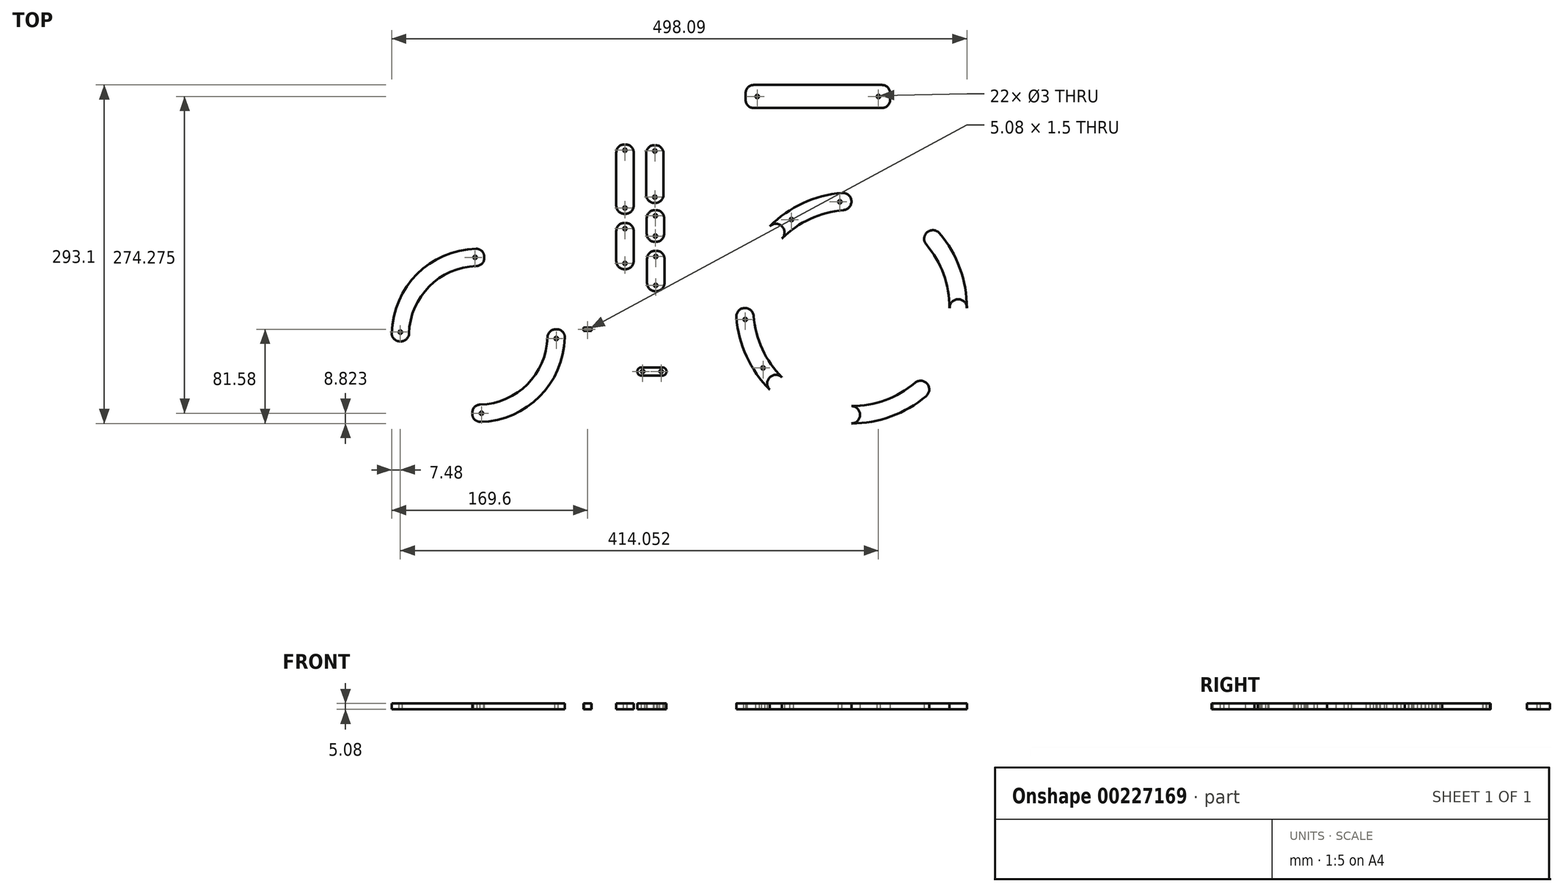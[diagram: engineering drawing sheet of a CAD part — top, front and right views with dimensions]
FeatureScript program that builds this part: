
annotation { "Feature Type Name" : "Feature", "Feature Type Description" : "" }
export const myFeature = defineFeature(function(context is Context, id is Id, definition is map)
    precondition{}
    {
        {
            var Q0;
            Q0=qCreatedBy(makeId("Top.planeOp"),FACE);
            var sketch = newSketch(context, id + "F0", { "sketchPlane" : qUnion([Q0])});
            skCircle(sketch, "E0", {"center": v(-65.55, 15.91) * mm, "radius": 75 * mm});
            skCircle(sketch, "E1", {"center": v(-65.55, 15.91) * mm, "radius": 60 * mm});
            skCircle(sketch, "E2", {"center": v(-68.33, 83.41) * mm, "radius": 1.5 * mm});
            skCircle(sketch, "E3", {"center": v(-133.05, 18.7) * mm, "radius": 1.5 * mm});
            skLineSegment(sketch, "E4", {"start": v(-140.37, 10.7) * mm, "end": v(-125.32, 10.7) * mm});
            skPoint(sketch, "E4.startSnap0", {"position": v(-133.05, 10.7) * mm});
            skLineSegment(sketch, "E5", {"start": v(-60.33, 90.73) * mm, "end": v(-60.33, 75.69) * mm});
            skPoint(sketch, "E5.startSnap0", {"position": v(-60.33, 83.41) * mm});
            skCircle(sketch, "E6", {"center": v(1.95, 13.13) * mm, "radius": 1.5 * mm});
            skCircle(sketch, "E7", {"center": v(-62.77, -51.59) * mm, "radius": 1.5 * mm});
            skLineSegment(sketch, "E8", {"start": v(-70.77, -43.86) * mm, "end": v(-70.77, -58.9) * mm});
            skPoint(sketch, "E8.startSnap0", {"position": v(-70.77, -51.59) * mm});
            skPoint(sketch, "E8.endSnap0", {"position": v(-70.77, -51.59) * mm});
            skPoint(sketch, "E9.startSnap0", {"position": v(1.95, 21.13) * mm});
            skLineSegment(sketch, "E10", {"start": v(-5.78, 21.13) * mm, "end": v(9.27, 21.13) * mm});
            skLineSegment(sketch, "E11.bottom", {"start": v(32.57, 19.67) * mm, "end": v(25.57, 19.67) * mm});
            skLineSegment(sketch, "E11.top", {"start": v(32.57, 22.67) * mm, "end": v(25.57, 22.67) * mm});
            skLineSegment(sketch, "E11.left", {"start": v(32.57, 19.67) * mm, "end": v(32.57, 22.67) * mm});
            skLineSegment(sketch, "E11.right", {"start": v(25.57, 19.67) * mm, "end": v(25.57, 22.67) * mm});
            skPoint(sketch, "E11.middle", {"position": v(29.07, 21.17) * mm});
            skLineSegment(sketch, "E12.bottom", {"start": v(31.61, 21.92) * mm, "end": v(26.53, 21.92) * mm});
            skLineSegment(sketch, "E12.top", {"start": v(31.61, 20.42) * mm, "end": v(26.53, 20.42) * mm});
            skLineSegment(sketch, "E12.left", {"start": v(31.61, 21.92) * mm, "end": v(31.61, 20.42) * mm});
            skLineSegment(sketch, "E12.right", {"start": v(26.53, 21.92) * mm, "end": v(26.53, 20.42) * mm});
            skLineSegment(sketch, "E13.bottom", {"start": v(97.3, -11.9) * mm, "end": v(72.3, -11.9) * mm});
            skLineSegment(sketch, "E13.top", {"start": v(97.3, -18.9) * mm, "end": v(72.3, -18.9) * mm});
            skLineSegment(sketch, "E13.left", {"start": v(97.3, -11.9) * mm, "end": v(97.3, -18.9) * mm});
            skLineSegment(sketch, "E13.right", {"start": v(72.3, -11.9) * mm, "end": v(72.3, -18.9) * mm});
            skPoint(sketch, "E13.middle", {"position": v(84.8, -15.4) * mm});
            skCircle(sketch, "E14", {"center": v(92.8, -15.4) * mm, "radius": 1.5 * mm});
            skLineSegment(sketch, "E15", {"start": v(84.8, -11.9) * mm, "end": v(84.8, -18.9) * mm});
            skCircle(sketch, "E16.MirrorC", {"center": v(76.8, -15.4) * mm, "radius": 1.5 * mm});
            skCircle(sketch, "E17", {"center": v(257.56, 39.59) * mm, "radius": 100 * mm});
            skCircle(sketch, "E18", {"center": v(257.56, 39.59) * mm, "radius": 85 * mm});
            skLineSegment(sketch, "E19", {"start": v(257.56, 39.59) * mm, "end": v(257.56, 139.59) * mm});
            skLineSegment(sketch, "E20", {"start": v(257.56, 39.59) * mm, "end": v(157.56, 39.59) * mm});
            skLineSegment(sketch, "E21", {"start": v(257.56, 39.59) * mm, "end": v(257.56, -60.41) * mm});
            skLineSegment(sketch, "E22", {"start": v(257.56, 39.59) * mm, "end": v(357.56, 39.59) * mm});
            skLineSegment(sketch, "E23", {"start": v(257.56, 39.59) * mm, "end": v(186.85, 110.3) * mm});
            skLineSegment(sketch, "E24.MirrorCS", {"start": v(257.56, 39.59) * mm, "end": v(328.28, 110.3) * mm});
            skLineSegment(sketch, "E25.MirrorCS", {"start": v(257.56, 39.59) * mm, "end": v(328.28, -31.13) * mm});
            skLineSegment(sketch, "E26.MirrorCS", {"start": v(257.56, 39.59) * mm, "end": v(186.85, -31.13) * mm});
            skArc(sketch, "E27", {"start": v(197.46, -20.52) * mm, "mid": v(186.85, -20.52) * mm, "end": v(186.85, -31.13) * mm});
            skArc(sketch, "E28", {"start": v(257.56, -60.41) * mm, "mid": v(265.06, -52.91) * mm, "end": v(257.56, -45.41) * mm});
            skArc(sketch, "E29", {"start": v(357.56, 39.59) * mm, "mid": v(350.06, 47.09) * mm, "end": v(342.56, 39.59) * mm});
            skArc(sketch, "E30", {"start": v(197.46, 99.69) * mm, "mid": v(197.46, 110.3) * mm, "end": v(186.85, 110.3) * mm});
            skCircle(sketch, "E31", {"center": v(257.56, 39.59) * mm, "radius": 92.5 * mm, "construction": true});
            skCircle(sketch, "E32", {"center": v(205.65, 116.14) * mm, "radius": 1.5 * mm});
            skCircle(sketch, "E33", {"center": v(247.56, 131.54) * mm, "radius": 1.5 * mm});
            skCircle(sketch, "E34", {"center": v(181, -12.33) * mm, "radius": 1.5 * mm});
            skCircle(sketch, "E35", {"center": v(165.6, 29.59) * mm, "radius": 1.5 * mm});
            skLineSegment(sketch, "E36.bottom", {"start": v(53.97, 181.17) * mm, "end": v(68.97, 181.17) * mm});
            skLineSegment(sketch, "E36.top", {"start": v(53.97, 121.17) * mm, "end": v(68.97, 121.17) * mm});
            skLineSegment(sketch, "E36.left", {"start": v(53.97, 181.17) * mm, "end": v(53.97, 121.17) * mm});
            skLineSegment(sketch, "E36.right", {"start": v(68.97, 181.17) * mm, "end": v(68.97, 121.17) * mm});
            skLineSegment(sketch, "E37.bottom", {"start": v(53.97, 113.23) * mm, "end": v(68.97, 113.23) * mm});
            skLineSegment(sketch, "E37.top", {"start": v(53.97, 73.23) * mm, "end": v(68.97, 73.23) * mm});
            skLineSegment(sketch, "E37.left", {"start": v(53.97, 113.23) * mm, "end": v(53.97, 73.23) * mm});
            skLineSegment(sketch, "E37.right", {"start": v(68.97, 113.23) * mm, "end": v(68.97, 73.23) * mm});
            skLineSegment(sketch, "E38.bottom", {"start": v(80.64, 89.11) * mm, "end": v(95.64, 89.11) * mm});
            skLineSegment(sketch, "E38.top", {"start": v(80.64, 54.11) * mm, "end": v(95.64, 54.11) * mm});
            skLineSegment(sketch, "E38.left", {"start": v(80.64, 89.11) * mm, "end": v(80.64, 54.11) * mm});
            skLineSegment(sketch, "E38.right", {"start": v(95.64, 89.11) * mm, "end": v(95.64, 54.11) * mm});
            skCircle(sketch, "E39", {"center": v(61.47, 176.17) * mm, "radius": 1.5 * mm});
            skPoint(sketch, "E39.centerSnap0", {"position": v(61.47, 181.17) * mm});
            skLineSegment(sketch, "E40", {"start": v(53.97, 151.17) * mm, "end": v(68.97, 151.17) * mm, "construction": true});
            skCircle(sketch, "E41.MirrorC", {"center": v(61.47, 126.17) * mm, "radius": 1.5 * mm});
            skCircle(sketch, "E42", {"center": v(88.14, 84.11) * mm, "radius": 1.5 * mm});
            skPoint(sketch, "E42.centerSnap0", {"position": v(88.14, 89.11) * mm});
            skLineSegment(sketch, "E43", {"start": v(80.64, 71.61) * mm, "end": v(95.64, 71.61) * mm, "construction": true});
            skCircle(sketch, "E44.MirrorC", {"center": v(88.14, 59.11) * mm, "radius": 1.5 * mm});
            skLineSegment(sketch, "E45", {"start": v(53.97, 93.23) * mm, "end": v(68.97, 93.23) * mm, "construction": true});
            skCircle(sketch, "E46", {"center": v(61.47, 108.23) * mm, "radius": 1.5 * mm});
            skPoint(sketch, "E46.centerSnap0", {"position": v(61.47, 113.23) * mm});
            skCircle(sketch, "E47.MirrorC", {"center": v(61.47, 78.23) * mm, "radius": 1.5 * mm});
            skPoint(sketch, "E48.centerSnap0", {"position": v(114.78, 118.5) * mm});
            skLineSegment(sketch, "E49", {"start": v(87.84, 119.35) * mm, "end": v(87.84, 101.85) * mm});
            skCircle(sketch, "E50", {"center": v(87.84, 119.35) * mm, "radius": 1.5 * mm});
            skCircle(sketch, "E51", {"center": v(87.84, 101.85) * mm, "radius": 1.5 * mm});
            skLineSegment(sketch, "E52.bottom", {"start": v(95.34, 124.35) * mm, "end": v(80.34, 124.35) * mm});
            skLineSegment(sketch, "E52.top", {"start": v(95.34, 96.85) * mm, "end": v(80.34, 96.85) * mm});
            skLineSegment(sketch, "E52.left", {"start": v(95.34, 124.35) * mm, "end": v(95.34, 96.85) * mm});
            skLineSegment(sketch, "E52.right", {"start": v(80.34, 124.35) * mm, "end": v(80.34, 96.85) * mm});
            skPoint(sketch, "E52.middle", {"position": v(87.84, 110.6) * mm});
            skLineSegment(sketch, "E53.bottom", {"start": v(79.83, 180.55) * mm, "end": v(94.83, 180.55) * mm});
            skLineSegment(sketch, "E53.top", {"start": v(79.83, 130.55) * mm, "end": v(94.83, 130.55) * mm});
            skLineSegment(sketch, "E53.left", {"start": v(79.83, 180.55) * mm, "end": v(79.83, 130.55) * mm});
            skLineSegment(sketch, "E53.right", {"start": v(94.83, 180.55) * mm, "end": v(94.83, 130.55) * mm});
            skCircle(sketch, "E54", {"center": v(87.33, 175.55) * mm, "radius": 1.5 * mm});
            skPoint(sketch, "E54.centerSnap0", {"position": v(87.33, 180.55) * mm});
            skLineSegment(sketch, "E55", {"start": v(79.83, 155.55) * mm, "end": v(94.83, 155.55) * mm, "construction": true});
            skCircle(sketch, "E56.MirrorC", {"center": v(87.33, 135.55) * mm, "radius": 1.5 * mm});
            skLineSegment(sketch, "E57.bottom", {"start": v(166, 232.69) * mm, "end": v(291, 232.69) * mm});
            skLineSegment(sketch, "E57.top", {"start": v(166, 212.69) * mm, "end": v(291, 212.69) * mm});
            skLineSegment(sketch, "E57.left", {"start": v(166, 232.69) * mm, "end": v(166, 212.69) * mm});
            skLineSegment(sketch, "E57.right", {"start": v(291, 232.69) * mm, "end": v(291, 212.69) * mm});
            skCircle(sketch, "E58", {"center": v(176, 222.69) * mm, "radius": 1.5 * mm});
            skPoint(sketch, "E58.centerSnap0", {"position": v(166, 222.69) * mm});
            skLineSegment(sketch, "E59", {"start": v(228.5, 232.69) * mm, "end": v(228.5, 212.69) * mm, "construction": true});
            skCircle(sketch, "E60.MirrorC", {"center": v(281, 222.69) * mm, "radius": 1.5 * mm});
            skSolve(sketch);
        }
        {
            var Q0;
            {var subQ0=sQuery(id+"F0.wireOp",EDGE,"hphmZsM6-x4Mk-0MsM-bUp3-fff5A3cwXpPa");Q0=makeQuery(id+"F0.imprint","IMPRINT",FACE,{"disambiguationData":[TD([[makeQuery(id+"F0.imprint","IMPRINT",EDGE,{"derivedFrom":subQ0}),1.0]])]});}
            var Q1;
            Q1=makeQuery(id+"F0.imprint","IMPRINT",FACE,{"disambiguationData":[TD([[makeQuery(id+"F0.imprint","IMPRINT",EDGE,{"derivedFrom":sQuery(id+"F0.wireOp",EDGE,"E2")}),-1.0]])]});
            var Q2;
            Q2=makeQuery(id+"F0.imprint","IMPRINT",FACE,{"disambiguationData":[TD([[makeQuery(id+"F0.imprint","IMPRINT",EDGE,{"derivedFrom":sQuery(id+"F0.wireOp",EDGE,"E6")}),-1.0]])]});
            var Q3;
            {var subQ0=sQuery(id+"F0.wireOp",EDGE,"E9");Q3=makeQuery(id+"F0.imprint","IMPRINT",FACE,{"disambiguationData":[TD([[makeQuery(id+"F0.imprint","IMPRINT",EDGE,{"derivedFrom":subQ0}),1.0]])]});}
            var Q4;
            Q4=makeQuery(id+"F0.imprint","IMPRINT",FACE,{"disambiguationData":[TD([[makeQuery(id+"F0.imprint","IMPRINT",EDGE,{"derivedFrom":sQuery(id+"F0.wireOp",EDGE,"E11.bottom")}),-1.0]])]});
            var Q5;
            {var subQ1=sQuery(id+"F0.wireOp",EDGE,"E13.right");Q5=makeQuery(id+"F0.imprint","IMPRINT",FACE,{"disambiguationData":[TD([[makeQuery(id+"F0.imprint","IMPRINT",EDGE,{"derivedFrom":subQ1}),1.0]])]});}
            var Q6;
            {var subQ0=sQuery(id+"F0.wireOp",EDGE,"E13.left");Q6=makeQuery(id+"F0.imprint","IMPRINT",FACE,{"disambiguationData":[TD([[makeQuery(id+"F0.imprint","IMPRINT",EDGE,{"derivedFrom":subQ0}),-1.0]])]});}
            var Q7;
            {var subQ0=sQuery(id+"F0.wireOp",EDGE,"E19");var subQ1=sQuery(id+"F0.wireOp",EDGE,"E17");var subQ2=makeQuery(id+"F0.imprint","INTERSECT",VERTEX,{"derivedFrom":[subQ1,subQ0]});Q7=makeQuery(id+"F0.imprint","IMPRINT",FACE,{"disambiguationData":[TD([[makeQuery(id+"F0.imprint","IMPRINT",EDGE,{"disambiguationData":[TD([[subQ2,-1.0]])],"derivedFrom":subQ1}),1.0]])]});}
            var Q8;
            {var subQ0=sQuery(id+"F0.wireOp",EDGE,"E22");var subQ1=sQuery(id+"F0.wireOp",EDGE,"E17");var subQ2=makeQuery(id+"F0.imprint","INTERSECT",VERTEX,{"derivedFrom":[subQ1,subQ0]});Q8=makeQuery(id+"F0.imprint","IMPRINT",FACE,{"disambiguationData":[TD([[makeQuery(id+"F0.imprint","IMPRINT",EDGE,{"disambiguationData":[TD([[subQ2,-1.0]])],"derivedFrom":subQ1}),1.0]])]});}
            var Q9;
            {var subQ0=sQuery(id+"F0.wireOp",EDGE,"E20");var subQ1=sQuery(id+"F0.wireOp",EDGE,"E17");var subQ2=makeQuery(id+"F0.imprint","INTERSECT",VERTEX,{"derivedFrom":[subQ1,subQ0]});Q9=makeQuery(id+"F0.imprint","IMPRINT",FACE,{"disambiguationData":[TD([[makeQuery(id+"F0.imprint","IMPRINT",EDGE,{"disambiguationData":[TD([[subQ2,-1.0]])],"derivedFrom":subQ1}),1.0]])]});}
            var Q10;
            {var subQ0=sQuery(id+"F0.wireOp",EDGE,"E21");var subQ1=sQuery(id+"F0.wireOp",EDGE,"E17");var subQ2=makeQuery(id+"F0.imprint","INTERSECT",VERTEX,{"derivedFrom":[subQ1,subQ0]});Q10=makeQuery(id+"F0.imprint","IMPRINT",FACE,{"disambiguationData":[TD([[makeQuery(id+"F0.imprint","IMPRINT",EDGE,{"disambiguationData":[TD([[subQ2,-1.0]])],"derivedFrom":subQ1}),1.0]])]});}
            var Q11;
            Q11=makeQuery(id+"F0.imprint","IMPRINT",FACE,{"disambiguationData":[TD([[makeQuery(id+"F0.imprint","IMPRINT",EDGE,{"derivedFrom":sQuery(id+"F0.wireOp",EDGE,"E36.bottom")}),-1.0]])]});
            var Q12;
            Q12=makeQuery(id+"F0.imprint","IMPRINT",FACE,{"disambiguationData":[TD([[makeQuery(id+"F0.imprint","IMPRINT",EDGE,{"derivedFrom":sQuery(id+"F0.wireOp",EDGE,"E37.bottom")}),-1.0]])]});
            var Q13;
            Q13=makeQuery(id+"F0.imprint","IMPRINT",FACE,{"disambiguationData":[TD([[makeQuery(id+"F0.imprint","IMPRINT",EDGE,{"derivedFrom":sQuery(id+"F0.wireOp",EDGE,"E38.bottom")}),-1.0]])]});
            var Q14;
            Q14=makeQuery(id+"F0.imprint","IMPRINT",FACE,{"disambiguationData":[TD([[makeQuery(id+"F0.imprint","IMPRINT",EDGE,{"derivedFrom":sQuery(id+"F0.wireOp",EDGE,"E50")}),-1.0]])]});
            var Q15;
            Q15=makeQuery(id+"F0.imprint","IMPRINT",FACE,{"disambiguationData":[TD([[makeQuery(id+"F0.imprint","IMPRINT",EDGE,{"derivedFrom":sQuery(id+"F0.wireOp",EDGE,"E53.bottom")}),-1.0]])]});
            var Q16;
            Q16=makeQuery(id+"F0.imprint","IMPRINT",FACE,{"disambiguationData":[TD([[makeQuery(id+"F0.imprint","IMPRINT",EDGE,{"derivedFrom":sQuery(id+"F0.wireOp",EDGE,"E57.bottom")}),-1.0]])]});
            extrude(context, id + "F1", {"entities" : qUnion([Q0, Q1, Q2, Q3, Q4, Q5, Q6, Q7, Q8, Q9, Q10, Q11, Q12, Q13, Q14, Q15, Q16]), "depth" : 5.08 * mm, "offsetDistance" : 25 * mm});
        }
        {
            var Q0;
            Q0=makeQuery(id+"F1.opExtrude","SWEPT_EDGE",EDGE,{"disambiguationData":[OSD([sQuery(id+"F0.wireOp",EDGE,"E0"),sQuery(id+"F0.wireOp",EDGE,"E4")])]});
            var Q1;
            Q1=makeQuery(id+"F1.opExtrude","SWEPT_EDGE",EDGE,{"disambiguationData":[OSD([sQuery(id+"F0.wireOp",EDGE,"E1"),sQuery(id+"F0.wireOp",EDGE,"E4")])]});
            var Q2;
            Q2=makeQuery(id+"F1.opExtrude","SWEPT_EDGE",EDGE,{"disambiguationData":[OSD([sQuery(id+"F0.wireOp",EDGE,"E0"),sQuery(id+"F0.wireOp",EDGE,"E5")])]});
            var Q3;
            Q3=makeQuery(id+"F1.opExtrude","SWEPT_EDGE",EDGE,{"disambiguationData":[OSD([sQuery(id+"F0.wireOp",EDGE,"E1"),sQuery(id+"F0.wireOp",EDGE,"E5")])]});
            var Q4;
            Q4=makeQuery(id+"F1.opExtrude","SWEPT_EDGE",EDGE,{"disambiguationData":[OSD([sQuery(id+"F0.wireOp",EDGE,"E1"),sQuery(id+"F0.wireOp",EDGE,"E10")])]});
            var Q5;
            Q5=makeQuery(id+"F1.opExtrude","SWEPT_EDGE",EDGE,{"disambiguationData":[OSD([sQuery(id+"F0.wireOp",EDGE,"E0"),sQuery(id+"F0.wireOp",EDGE,"E10")])]});
            var Q6;
            Q6=makeQuery(id+"F1.opExtrude","SWEPT_EDGE",EDGE,{"disambiguationData":[OSD([sQuery(id+"F0.wireOp",EDGE,"E1"),sQuery(id+"F0.wireOp",EDGE,"E8")])]});
            var Q7;
            Q7=makeQuery(id+"F1.opExtrude","SWEPT_EDGE",EDGE,{"disambiguationData":[OSD([sQuery(id+"F0.wireOp",EDGE,"E0"),sQuery(id+"F0.wireOp",EDGE,"E8")])]});
            var Q8;
            Q8=makeQuery(id+"F1.opExtrude","SWEPT_EDGE",EDGE,{"disambiguationData":[OSD([sQuery(id+"F0.wireOp",EDGE,"E36.bottom"),sQuery(id+"F0.wireOp",EDGE,"E36.right")])]});
            var Q9;
            Q9=makeQuery(id+"F1.opExtrude","SWEPT_EDGE",EDGE,{"disambiguationData":[OSD([sQuery(id+"F0.wireOp",EDGE,"E36.bottom"),sQuery(id+"F0.wireOp",EDGE,"E36.left")])]});
            var Q10;
            Q10=makeQuery(id+"F1.opExtrude","SWEPT_EDGE",EDGE,{"disambiguationData":[OSD([sQuery(id+"F0.wireOp",EDGE,"E36.top"),sQuery(id+"F0.wireOp",EDGE,"E36.left")])]});
            var Q11;
            Q11=makeQuery(id+"F1.opExtrude","SWEPT_EDGE",EDGE,{"disambiguationData":[OSD([sQuery(id+"F0.wireOp",EDGE,"E36.top"),sQuery(id+"F0.wireOp",EDGE,"E36.right")])]});
            var Q12;
            Q12=makeQuery(id+"F1.opExtrude","SWEPT_EDGE",EDGE,{"disambiguationData":[OSD([sQuery(id+"F0.wireOp",EDGE,"E37.bottom"),sQuery(id+"F0.wireOp",EDGE,"E37.left")])]});
            var Q13;
            Q13=makeQuery(id+"F1.opExtrude","SWEPT_EDGE",EDGE,{"disambiguationData":[OSD([sQuery(id+"F0.wireOp",EDGE,"E37.bottom"),sQuery(id+"F0.wireOp",EDGE,"E37.right")])]});
            var Q14;
            Q14=makeQuery(id+"F1.opExtrude","SWEPT_EDGE",EDGE,{"disambiguationData":[OSD([sQuery(id+"F0.wireOp",EDGE,"E37.top"),sQuery(id+"F0.wireOp",EDGE,"E37.right")])]});
            var Q15;
            Q15=makeQuery(id+"F1.opExtrude","SWEPT_EDGE",EDGE,{"disambiguationData":[OSD([sQuery(id+"F0.wireOp",EDGE,"E37.top"),sQuery(id+"F0.wireOp",EDGE,"E37.left")])]});
            var Q16;
            Q16=makeQuery(id+"F1.opExtrude","SWEPT_EDGE",EDGE,{"disambiguationData":[OSD([sQuery(id+"F0.wireOp",EDGE,"E38.top"),sQuery(id+"F0.wireOp",EDGE,"E38.right")])]});
            var Q17;
            Q17=makeQuery(id+"F1.opExtrude","SWEPT_EDGE",EDGE,{"disambiguationData":[OSD([sQuery(id+"F0.wireOp",EDGE,"E38.top"),sQuery(id+"F0.wireOp",EDGE,"E38.left")])]});
            var Q18;
            Q18=makeQuery(id+"F1.opExtrude","SWEPT_EDGE",EDGE,{"disambiguationData":[OSD([sQuery(id+"F0.wireOp",EDGE,"E38.bottom"),sQuery(id+"F0.wireOp",EDGE,"E38.left")])]});
            var Q19;
            Q19=makeQuery(id+"F1.opExtrude","SWEPT_EDGE",EDGE,{"disambiguationData":[OSD([sQuery(id+"F0.wireOp",EDGE,"E38.bottom"),sQuery(id+"F0.wireOp",EDGE,"E38.right")])]});
            var Q20;
            Q20=makeQuery(id+"F1.opExtrude","SWEPT_EDGE",EDGE,{"disambiguationData":[OSD([sQuery(id+"F0.wireOp",EDGE,"E52.bottom"),sQuery(id+"F0.wireOp",EDGE,"E52.right")])]});
            var Q21;
            Q21=makeQuery(id+"F1.opExtrude","SWEPT_EDGE",EDGE,{"disambiguationData":[OSD([sQuery(id+"F0.wireOp",EDGE,"E52.bottom"),sQuery(id+"F0.wireOp",EDGE,"E52.left")])]});
            var Q22;
            Q22=makeQuery(id+"F1.opExtrude","SWEPT_EDGE",EDGE,{"disambiguationData":[OSD([sQuery(id+"F0.wireOp",EDGE,"E52.top"),sQuery(id+"F0.wireOp",EDGE,"E52.left")])]});
            var Q23;
            Q23=makeQuery(id+"F1.opExtrude","SWEPT_EDGE",EDGE,{"disambiguationData":[OSD([sQuery(id+"F0.wireOp",EDGE,"E52.top"),sQuery(id+"F0.wireOp",EDGE,"E52.right")])]});
            var Q24;
            Q24=makeQuery(id+"F1.opExtrude","SWEPT_EDGE",EDGE,{"disambiguationData":[OSD([sQuery(id+"F0.wireOp",EDGE,"E53.top"),sQuery(id+"F0.wireOp",EDGE,"E53.right")])]});
            var Q25;
            Q25=makeQuery(id+"F1.opExtrude","SWEPT_EDGE",EDGE,{"disambiguationData":[OSD([sQuery(id+"F0.wireOp",EDGE,"E53.top"),sQuery(id+"F0.wireOp",EDGE,"E53.left")])]});
            var Q26;
            Q26=makeQuery(id+"F1.opExtrude","SWEPT_EDGE",EDGE,{"disambiguationData":[OSD([sQuery(id+"F0.wireOp",EDGE,"E53.bottom"),sQuery(id+"F0.wireOp",EDGE,"E53.left")])]});
            var Q27;
            Q27=makeQuery(id+"F1.opExtrude","SWEPT_EDGE",EDGE,{"disambiguationData":[OSD([sQuery(id+"F0.wireOp",EDGE,"E53.bottom"),sQuery(id+"F0.wireOp",EDGE,"E53.right")])]});
            var Q28;
            Q28=makeQuery(id+"F1.opExtrude","SWEPT_EDGE",EDGE,{"disambiguationData":[OSD([sQuery(id+"F0.wireOp",EDGE,"E57.bottom"),sQuery(id+"F0.wireOp",EDGE,"E57.left")])]});
            var Q29;
            Q29=makeQuery(id+"F1.opExtrude","SWEPT_EDGE",EDGE,{"disambiguationData":[OSD([sQuery(id+"F0.wireOp",EDGE,"E57.top"),sQuery(id+"F0.wireOp",EDGE,"E57.left")])]});
            var Q30;
            Q30=makeQuery(id+"F1.opExtrude","SWEPT_EDGE",EDGE,{"disambiguationData":[OSD([sQuery(id+"F0.wireOp",EDGE,"E57.bottom"),sQuery(id+"F0.wireOp",EDGE,"E57.right")])]});
            var Q31;
            Q31=makeQuery(id+"F1.opExtrude","SWEPT_EDGE",EDGE,{"disambiguationData":[OSD([sQuery(id+"F0.wireOp",EDGE,"E57.top"),sQuery(id+"F0.wireOp",EDGE,"E57.right")])]});
            fillet(context, id + "F2", {"entities" : qUnion([Q0, Q1, Q2, Q3, Q4, Q5, Q6, Q7, Q8, Q9, Q10, Q11, Q12, Q13, Q14, Q15, Q16, Q17, Q18, Q19, Q20, Q21, Q22, Q23, Q24, Q25, Q26, Q27, Q28, Q29, Q30, Q31]), "radius" : 7 * mm, "tangentPropagation" : true, "allowEdgeOverflow" : false});
        }
        {
            var Q0;
            Q0=makeQuery(id+"F1.opExtrude","SWEPT_EDGE",EDGE,{"disambiguationData":[OSD([sQuery(id+"F0.wireOp",EDGE,"E13.bottom"),sQuery(id+"F0.wireOp",EDGE,"E13.right")])]});
            var Q1;
            Q1=makeQuery(id+"F1.opExtrude","SWEPT_EDGE",EDGE,{"disambiguationData":[OSD([sQuery(id+"F0.wireOp",EDGE,"E13.top"),sQuery(id+"F0.wireOp",EDGE,"E13.right")])]});
            var Q2;
            Q2=makeQuery(id+"F1.opExtrude","SWEPT_EDGE",EDGE,{"disambiguationData":[OSD([sQuery(id+"F0.wireOp",EDGE,"E13.bottom"),sQuery(id+"F0.wireOp",EDGE,"E13.left")])]});
            var Q3;
            Q3=makeQuery(id+"F1.opExtrude","SWEPT_EDGE",EDGE,{"disambiguationData":[OSD([sQuery(id+"F0.wireOp",EDGE,"E13.top"),sQuery(id+"F0.wireOp",EDGE,"E13.left")])]});
            fillet(context, id + "F3", {"entities" : qUnion([Q0, Q1, Q2, Q3]), "radius" : 3 * mm, "tangentPropagation" : true, "allowEdgeOverflow" : false});
        }
        {
            var Q0;
            Q0=makeQuery(id+"F1.opExtrude","SWEPT_EDGE",EDGE,{"disambiguationData":[OSD([sQuery(id+"F0.wireOp",EDGE,"E17"),sQuery(id+"F0.wireOp",EDGE,"E19")])]});
            var Q1;
            Q1=makeQuery(id+"F1.opExtrude","SWEPT_EDGE",EDGE,{"disambiguationData":[OSD([sQuery(id+"F0.wireOp",EDGE,"E18"),sQuery(id+"F0.wireOp",EDGE,"E19")])]});
            var Q2;
            Q2=makeQuery(id+"F1.opExtrude","SWEPT_EDGE",EDGE,{"disambiguationData":[OSD([sQuery(id+"F0.wireOp",EDGE,"E17"),sQuery(id+"F0.wireOp",EDGE,"E24.MirrorCS")])]});
            var Q3;
            Q3=makeQuery(id+"F1.opExtrude","SWEPT_EDGE",EDGE,{"disambiguationData":[OSD([sQuery(id+"F0.wireOp",EDGE,"E18"),sQuery(id+"F0.wireOp",EDGE,"E24.MirrorCS")])]});
            var Q4;
            Q4=makeQuery(id+"F1.opExtrude","SWEPT_EDGE",EDGE,{"disambiguationData":[OSD([sQuery(id+"F0.wireOp",EDGE,"E18"),sQuery(id+"F0.wireOp",EDGE,"E25.MirrorCS")])]});
            var Q5;
            Q5=makeQuery(id+"F1.opExtrude","SWEPT_EDGE",EDGE,{"disambiguationData":[OSD([sQuery(id+"F0.wireOp",EDGE,"E17"),sQuery(id+"F0.wireOp",EDGE,"E25.MirrorCS")])]});
            var Q6;
            Q6=makeQuery(id+"F1.opExtrude","SWEPT_EDGE",EDGE,{"disambiguationData":[OSD([sQuery(id+"F0.wireOp",EDGE,"E17"),sQuery(id+"F0.wireOp",EDGE,"E20")])]});
            var Q7;
            Q7=makeQuery(id+"F1.opExtrude","SWEPT_EDGE",EDGE,{"disambiguationData":[OSD([sQuery(id+"F0.wireOp",EDGE,"E18"),sQuery(id+"F0.wireOp",EDGE,"E20")])]});
            fillet(context, id + "F4", {"entities" : qUnion([Q0, Q1, Q2, Q3, Q4, Q5, Q6, Q7]), "radius" : 7.5 * mm, "tangentPropagation" : true, "allowEdgeOverflow" : false});
        }
    });
